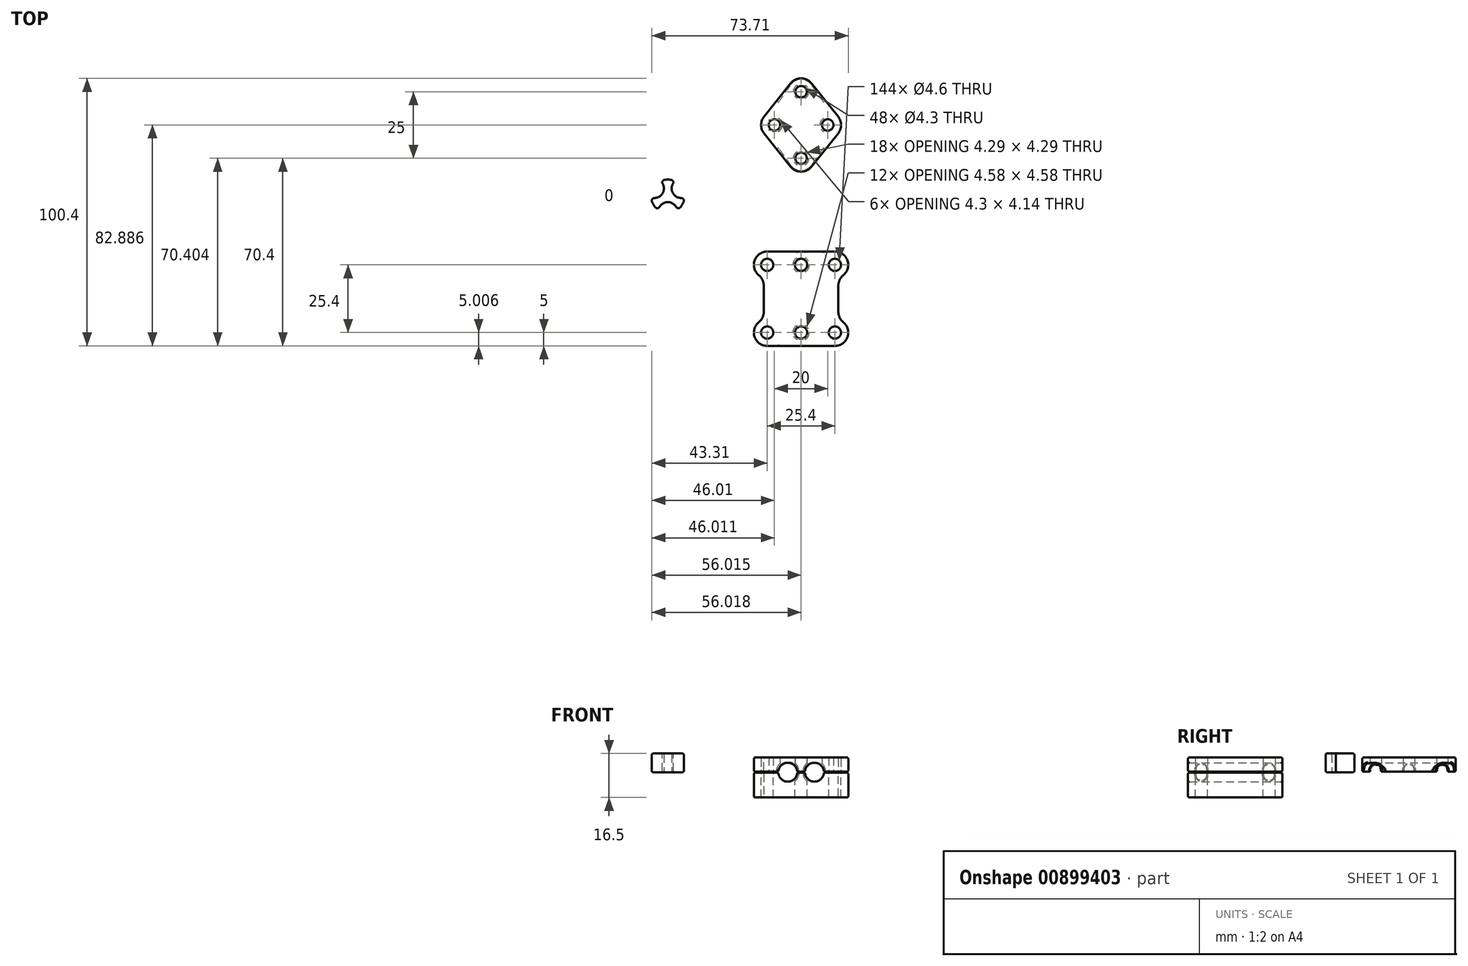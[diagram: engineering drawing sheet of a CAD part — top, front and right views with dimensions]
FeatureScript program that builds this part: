
annotation { "Feature Type Name" : "Feature", "Feature Type Description" : "" }
export const myFeature = defineFeature(function(context is Context, id is Id, definition is map)
    precondition{}
    {
        {
            var Q0;
            Q0=qCreatedBy(makeId("Top.planeOp"),FACE);
            var sketch = newSketch(context, id + "F0", { "sketchPlane" : qUnion([Q0])});
            skCircle(sketch, "E0", {"center": v(0, 45) * mm, "radius": 2.15 * mm});
            skCircle(sketch, "E1", {"center": v(-10, 32.5) * mm, "radius": 2.15 * mm});
            skCircle(sketch, "E2", {"center": v(10, 32.5) * mm, "radius": 2.15 * mm});
            skCircle(sketch, "E3", {"center": v(0, 20) * mm, "radius": 2.15 * mm});
            skArc(sketch, "E4", {"start": v(-13.9, 35.62) * mm, "mid": v(-15, 32.5) * mm, "end": v(-13.9, 29.38) * mm});
            skArc(sketch, "E5", {"start": v(-3.9, 16.88) * mm, "mid": v(0, 15) * mm, "end": v(3.9, 16.88) * mm});
            skArc(sketch, "E6", {"start": v(13.9, 29.38) * mm, "mid": v(15, 32.5) * mm, "end": v(13.9, 35.62) * mm});
            skArc(sketch, "E7", {"start": v(3.9, 48.12) * mm, "mid": v(0, 50) * mm, "end": v(-3.9, 48.12) * mm});
            skLineSegment(sketch, "E8", {"start": v(-3.9, 48.12) * mm, "end": v(-13.9, 35.62) * mm});
            skLineSegment(sketch, "E9", {"start": v(-13.9, 29.38) * mm, "end": v(-3.9, 16.88) * mm});
            skLineSegment(sketch, "E10", {"start": v(3.9, 16.88) * mm, "end": v(13.9, 29.38) * mm});
            skLineSegment(sketch, "E11", {"start": v(3.9, 48.12) * mm, "end": v(13.9, 35.62) * mm});
            skCircle(sketch, "E12", {"center": v(0, -20) * mm, "radius": 2.3 * mm});
            skCircle(sketch, "E13", {"center": v(0, -45.4) * mm, "radius": 2.3 * mm});
            skCircle(sketch, "E14", {"center": v(12.7, -20) * mm, "radius": 2.3 * mm});
            skCircle(sketch, "E15", {"center": v(12.7, -45.4) * mm, "radius": 2.3 * mm});
            skCircle(sketch, "E16", {"center": v(-12.7, -45.4) * mm, "radius": 2.3 * mm});
            skCircle(sketch, "E17", {"center": v(-12.7, -20) * mm, "radius": 2.3 * mm});
            skArc(sketch, "E18", {"start": v(-12.7, -15) * mm, "mid": v(-17.66, -19.34) * mm, "end": v(-14, -24.83) * mm});
            skArc(sketch, "E19", {"start": v(14, -24.83) * mm, "mid": v(17.66, -19.34) * mm, "end": v(12.7, -15) * mm});
            skArc(sketch, "E20", {"start": v(-14, -40.57) * mm, "mid": v(-17.66, -46.06) * mm, "end": v(-12.7, -50.4) * mm});
            skArc(sketch, "E21", {"start": v(12.7, -50.4) * mm, "mid": v(17.66, -46.06) * mm, "end": v(14, -40.57) * mm});
            skLineSegment(sketch, "E22", {"start": v(-14, -24.83) * mm, "end": v(-14, -40.57) * mm});
            skLineSegment(sketch, "E23", {"start": v(-12.7, -15) * mm, "end": v(12.7, -15) * mm});
            skLineSegment(sketch, "E24", {"start": v(14, -24.83) * mm, "end": v(14, -40.57) * mm});
            skLineSegment(sketch, "E25", {"start": v(-12.7, -50.4) * mm, "end": v(12.7, -50.4) * mm});
            skSolve(sketch);
        }
        {
            var Q0;
            Q0=makeQuery(id+"F0.imprint","IMPRINT",FACE,{"disambiguationData":[TD([[makeQuery(id+"F0.imprint","IMPRINT",EDGE,{"derivedFrom":sQuery(id+"F0.wireOp",EDGE,"E0")}),-1.0]])]});
            extrude(context, id + "F1", {"entities" : qUnion([Q0]), "depth" : 5.5 * mm, "offsetDistance" : 25 * mm, "hasSecondDirection" : true, "secondDirectionOppositeDirection" : false, "secondDirectionDepth" : 0.2 * mm});
        }
        {
            var Q0;
            Q0=makeQuery(id+"F0.imprint","IMPRINT",FACE,{"disambiguationData":[TD([[makeQuery(id+"F0.imprint","IMPRINT",EDGE,{"derivedFrom":sQuery(id+"F0.wireOp",EDGE,"E12")}),-1.0]])]});
            extrude(context, id + "F2", {"entities" : qUnion([Q0]), "depth" : 5.5 * mm, "offsetDistance" : 25 * mm, "hasSecondDirection" : true, "secondDirectionOppositeDirection" : false, "secondDirectionDepth" : 0.2 * mm});
        }
        {
            var Q0;
            Q0=makeQuery(id+"F0.imprint","IMPRINT",FACE,{"disambiguationData":[TD([[makeQuery(id+"F0.imprint","IMPRINT",EDGE,{"derivedFrom":sQuery(id+"F0.wireOp",EDGE,"E12")}),-1.0]])]});
            extrude(context, id + "F3", {"entities" : qUnion([Q0]), "oppositeDirection" : true, "depth" : 9.5 * mm, "offsetDistance" : 25 * mm, "hasSecondDirection" : true, "secondDirectionOppositeDirection" : true, "secondDirectionDepth" : 0.2 * mm});
        }
        {
            var Q0;
            Q0=qCreatedBy(makeId("Front.planeOp"),FACE);
            var sketch = newSketch(context, id + "F4", { "sketchPlane" : qUnion([Q0])});
            skCircle(sketch, "E26", {"center": v(5, 0) * mm, "radius": 3.55 * mm});
            skCircle(sketch, "E27.MirrorC", {"center": v(-5, 0) * mm, "radius": 3.55 * mm});
            skSolve(sketch);
        }
        {
            var Q0;
            Q0 = qSketchRegion(id + "F4", true);
            extrude(context, id + "F5", {"entities" : qUnion([Q0]), "operationType" : NewBodyOperationType.REMOVE, "endBound" : BoundingType.SYMMETRIC, "depth" : 200 * mm, "offsetDistance" : 25 * mm});
        }
        {
            var Q0;
            Q0=makeQuery(id+"F2.opExtrude","SWEPT_EDGE",EDGE,{"disambiguationData":[OSD([sQuery(id+"F0.wireOp",EDGE,"E18"),sQuery(id+"F0.wireOp",EDGE,"E22")])]});
            var Q1;
            Q1=makeQuery(id+"F2.opExtrude","SWEPT_EDGE",EDGE,{"disambiguationData":[OSD([sQuery(id+"F0.wireOp",EDGE,"E20"),sQuery(id+"F0.wireOp",EDGE,"E22")])]});
            var Q2;
            Q2=makeQuery(id+"F2.opExtrude","SWEPT_EDGE",EDGE,{"disambiguationData":[OSD([sQuery(id+"F0.wireOp",EDGE,"E19"),sQuery(id+"F0.wireOp",EDGE,"E24")])]});
            var Q3;
            Q3=makeQuery(id+"F2.opExtrude","SWEPT_EDGE",EDGE,{"disambiguationData":[OSD([sQuery(id+"F0.wireOp",EDGE,"E21"),sQuery(id+"F0.wireOp",EDGE,"E24")])]});
            var Q4;
            Q4=makeQuery(id+"F3.opExtrude","SWEPT_EDGE",EDGE,{"disambiguationData":[OSD([sQuery(id+"F0.wireOp",EDGE,"E18"),sQuery(id+"F0.wireOp",EDGE,"E22")])]});
            var Q5;
            Q5=makeQuery(id+"F3.opExtrude","SWEPT_EDGE",EDGE,{"disambiguationData":[OSD([sQuery(id+"F0.wireOp",EDGE,"E20"),sQuery(id+"F0.wireOp",EDGE,"E22")])]});
            var Q6;
            Q6=makeQuery(id+"F3.opExtrude","SWEPT_EDGE",EDGE,{"disambiguationData":[OSD([sQuery(id+"F0.wireOp",EDGE,"E19"),sQuery(id+"F0.wireOp",EDGE,"E24")])]});
            var Q7;
            Q7=makeQuery(id+"F3.opExtrude","SWEPT_EDGE",EDGE,{"disambiguationData":[OSD([sQuery(id+"F0.wireOp",EDGE,"E21"),sQuery(id+"F0.wireOp",EDGE,"E24")])]});
            fillet(context, id + "F6", {"entities" : qUnion([Q0, Q1, Q2, Q3, Q4, Q5, Q6, Q7]), "radius" : 5 * mm, "tangentPropagation" : true, "allowEdgeOverflow" : false});
        }
        {
            var Q0;
            Q0=makeQuery(id+"F1.opExtrude","CAP_EDGE",EDGE,{"disambiguationData":[OSD([sQuery(id+"F0.wireOp",EDGE,"E9")])],"isStart":false});
            var Q1;
            Q1=makeQuery(id+"F2.opExtrude","CAP_EDGE",EDGE,{"disambiguationData":[OSD([sQuery(id+"F0.wireOp",EDGE,"E22")])],"isStart":false});
            var Q2;
            {var subQ3=sQuery(id+"F0.wireOp",EDGE,"E12");Q2=makeQuery(id+"F5.boolean.opBoolean","COPY",FACE,{"disambiguationData":[TD([makeQuery(id+"F2.opExtrude","SWEPT_FACE",FACE,{"disambiguationData":[OSD([subQ3])]})])],"derivedFrom":makeQuery(id+"F5.opExtrude","SWEPT_FACE",FACE,{"disambiguationData":[OSD([sQuery(id+"F4.wireOp",EDGE,"E27.MirrorC")])]})});}
            var Q3;
            {var subQ3=sQuery(id+"F0.wireOp",EDGE,"E12");Q3=makeQuery(id+"F5.boolean.opBoolean","COPY",FACE,{"disambiguationData":[TD([makeQuery(id+"F2.opExtrude","SWEPT_FACE",FACE,{"disambiguationData":[OSD([subQ3])]})])],"derivedFrom":makeQuery(id+"F5.opExtrude","SWEPT_FACE",FACE,{"disambiguationData":[OSD([sQuery(id+"F4.wireOp",EDGE,"E26")])]})});}
            var Q4;
            {var subQ0=sQuery(id+"F0.wireOp",EDGE,"E12");var subQ1=sQuery(id+"F0.wireOp",EDGE,"E13");Q4=makeQuery(id+"F5.boolean.opBoolean","SPLIT",FACE,{"disambiguationData":[TD([makeQuery(id+"F2.opExtrude","SWEPT_FACE",FACE,{"disambiguationData":[OSD([subQ0])]}),makeQuery(id+"F2.opExtrude","SWEPT_FACE",FACE,{"disambiguationData":[OSD([subQ1])]}),makeQuery(id+"F5.opExtrude","SWEPT_FACE",FACE,{"disambiguationData":[OSD([sQuery(id+"F4.wireOp",EDGE,"E26")])]}),makeQuery(id+"F5.opExtrude","SWEPT_FACE",FACE,{"disambiguationData":[OSD([sQuery(id+"F4.wireOp",EDGE,"E27.MirrorC")])]})])],"derivedFrom":makeQuery(id+"F2.opExtrude","CAP_FACE",FACE,{"disambiguationData":[OSD([subQ0,subQ1,sQuery(id+"F0.wireOp",EDGE,"E14"),sQuery(id+"F0.wireOp",EDGE,"E15"),sQuery(id+"F0.wireOp",EDGE,"E16"),sQuery(id+"F0.wireOp",EDGE,"E17"),sQuery(id+"F0.wireOp",EDGE,"E18"),sQuery(id+"F0.wireOp",EDGE,"E19"),sQuery(id+"F0.wireOp",EDGE,"E20"),sQuery(id+"F0.wireOp",EDGE,"E21"),sQuery(id+"F0.wireOp",EDGE,"E22"),sQuery(id+"F0.wireOp",EDGE,"E23"),sQuery(id+"F0.wireOp",EDGE,"E24"),sQuery(id+"F0.wireOp",EDGE,"E25")])],"isStart":true})});}
            var Q5;
            {var subQ0=sQuery(id+"F0.wireOp",EDGE,"E13");var subQ1=sQuery(id+"F0.wireOp",EDGE,"E25");Q5=makeQuery(id+"F5.boolean.opBoolean","SPLIT",FACE,{"disambiguationData":[TD([makeQuery(id+"F2.opExtrude","SWEPT_FACE",FACE,{"disambiguationData":[OSD([subQ0])]}),makeQuery(id+"F2.opExtrude","SWEPT_FACE",FACE,{"disambiguationData":[OSD([subQ1])]}),makeQuery(id+"F5.opExtrude","SWEPT_FACE",FACE,{"disambiguationData":[OSD([sQuery(id+"F4.wireOp",EDGE,"E26")])]}),makeQuery(id+"F5.opExtrude","SWEPT_FACE",FACE,{"disambiguationData":[OSD([sQuery(id+"F4.wireOp",EDGE,"E27.MirrorC")])]})])],"derivedFrom":makeQuery(id+"F2.opExtrude","CAP_FACE",FACE,{"disambiguationData":[OSD([sQuery(id+"F0.wireOp",EDGE,"E12"),subQ0,sQuery(id+"F0.wireOp",EDGE,"E14"),sQuery(id+"F0.wireOp",EDGE,"E15"),sQuery(id+"F0.wireOp",EDGE,"E16"),sQuery(id+"F0.wireOp",EDGE,"E17"),sQuery(id+"F0.wireOp",EDGE,"E18"),sQuery(id+"F0.wireOp",EDGE,"E19"),sQuery(id+"F0.wireOp",EDGE,"E20"),sQuery(id+"F0.wireOp",EDGE,"E21"),sQuery(id+"F0.wireOp",EDGE,"E22"),sQuery(id+"F0.wireOp",EDGE,"E23"),sQuery(id+"F0.wireOp",EDGE,"E24"),subQ1])],"isStart":true})});}
            var Q6;
            {var subQ0=sQuery(id+"F0.wireOp",EDGE,"E12");var subQ1=sQuery(id+"F0.wireOp",EDGE,"E23");Q6=makeQuery(id+"F5.boolean.opBoolean","SPLIT",FACE,{"disambiguationData":[TD([makeQuery(id+"F2.opExtrude","SWEPT_FACE",FACE,{"disambiguationData":[OSD([subQ0])]}),makeQuery(id+"F2.opExtrude","SWEPT_FACE",FACE,{"disambiguationData":[OSD([subQ1])]}),makeQuery(id+"F5.opExtrude","SWEPT_FACE",FACE,{"disambiguationData":[OSD([sQuery(id+"F4.wireOp",EDGE,"E26")])]}),makeQuery(id+"F5.opExtrude","SWEPT_FACE",FACE,{"disambiguationData":[OSD([sQuery(id+"F4.wireOp",EDGE,"E27.MirrorC")])]})])],"derivedFrom":makeQuery(id+"F2.opExtrude","CAP_FACE",FACE,{"disambiguationData":[OSD([subQ0,sQuery(id+"F0.wireOp",EDGE,"E13"),sQuery(id+"F0.wireOp",EDGE,"E14"),sQuery(id+"F0.wireOp",EDGE,"E15"),sQuery(id+"F0.wireOp",EDGE,"E16"),sQuery(id+"F0.wireOp",EDGE,"E17"),sQuery(id+"F0.wireOp",EDGE,"E18"),sQuery(id+"F0.wireOp",EDGE,"E19"),sQuery(id+"F0.wireOp",EDGE,"E20"),sQuery(id+"F0.wireOp",EDGE,"E21"),sQuery(id+"F0.wireOp",EDGE,"E22"),subQ1,sQuery(id+"F0.wireOp",EDGE,"E24"),sQuery(id+"F0.wireOp",EDGE,"E25")])],"isStart":true})});}
            var Q7;
            {var subQ0=sQuery(id+"F0.wireOp",EDGE,"E25");var subQ1=sQuery(id+"F0.wireOp",EDGE,"E20");Q7=makeQuery(id+"F5.boolean.opBoolean","SPLIT",EDGE,{"disambiguationData":[TD([makeQuery(id+"F2.opExtrude","CAP_FACE",FACE,{"disambiguationData":[OSD([sQuery(id+"F0.wireOp",EDGE,"E12"),sQuery(id+"F0.wireOp",EDGE,"E13"),sQuery(id+"F0.wireOp",EDGE,"E14"),sQuery(id+"F0.wireOp",EDGE,"E15"),sQuery(id+"F0.wireOp",EDGE,"E16"),sQuery(id+"F0.wireOp",EDGE,"E17"),sQuery(id+"F0.wireOp",EDGE,"E18"),sQuery(id+"F0.wireOp",EDGE,"E19"),subQ1,sQuery(id+"F0.wireOp",EDGE,"E21"),sQuery(id+"F0.wireOp",EDGE,"E22"),sQuery(id+"F0.wireOp",EDGE,"E23"),sQuery(id+"F0.wireOp",EDGE,"E24"),subQ0])],"isStart":true}),makeQuery(id+"F2.opExtrude","SWEPT_FACE",FACE,{"disambiguationData":[OSD([subQ1])]}),makeQuery(id+"F2.opExtrude","SWEPT_FACE",FACE,{"disambiguationData":[OSD([subQ0])]}),makeQuery(id+"F5.opExtrude","SWEPT_FACE",FACE,{"disambiguationData":[OSD([sQuery(id+"F4.wireOp",EDGE,"E27.MirrorC")])]})])],"derivedFrom":makeQuery(id+"F2.opExtrude","CAP_EDGE",EDGE,{"disambiguationData":[OSD([subQ0])],"isStart":true})});}
            var Q8;
            Q8=makeQuery(id+"F2.opExtrude","CAP_EDGE",EDGE,{"disambiguationData":[OSD([sQuery(id+"F0.wireOp",EDGE,"E21")])],"isStart":true});
            var Q9;
            {var subQ6=sQuery(id+"F0.wireOp",EDGE,"E0");Q9=makeQuery(id+"F5.boolean.opBoolean","COPY",FACE,{"disambiguationData":[TD([makeQuery(id+"F1.opExtrude","SWEPT_FACE",FACE,{"disambiguationData":[OSD([subQ6])]})])],"derivedFrom":makeQuery(id+"F5.opExtrude","SWEPT_FACE",FACE,{"disambiguationData":[OSD([sQuery(id+"F4.wireOp",EDGE,"E26")])]})});}
            var Q10;
            {var subQ6=sQuery(id+"F0.wireOp",EDGE,"E0");Q10=makeQuery(id+"F5.boolean.opBoolean","COPY",FACE,{"disambiguationData":[TD([makeQuery(id+"F1.opExtrude","SWEPT_FACE",FACE,{"disambiguationData":[OSD([subQ6])]})])],"derivedFrom":makeQuery(id+"F5.opExtrude","SWEPT_FACE",FACE,{"disambiguationData":[OSD([sQuery(id+"F4.wireOp",EDGE,"E27.MirrorC")])]})});}
            var Q11;
            {var subQ0=sQuery(id+"F0.wireOp",EDGE,"E3");var subQ1=sQuery(id+"F0.wireOp",EDGE,"E5");Q11=makeQuery(id+"F5.boolean.opBoolean","SPLIT",FACE,{"disambiguationData":[TD([makeQuery(id+"F1.opExtrude","SWEPT_FACE",FACE,{"disambiguationData":[OSD([subQ0])]}),makeQuery(id+"F1.opExtrude","SWEPT_FACE",FACE,{"disambiguationData":[OSD([subQ1])]}),makeQuery(id+"F5.opExtrude","SWEPT_FACE",FACE,{"disambiguationData":[OSD([sQuery(id+"F4.wireOp",EDGE,"E26")])]}),makeQuery(id+"F5.opExtrude","SWEPT_FACE",FACE,{"disambiguationData":[OSD([sQuery(id+"F4.wireOp",EDGE,"E27.MirrorC")])]})])],"derivedFrom":makeQuery(id+"F1.opExtrude","CAP_FACE",FACE,{"disambiguationData":[OSD([sQuery(id+"F0.wireOp",EDGE,"E0"),sQuery(id+"F0.wireOp",EDGE,"E1"),sQuery(id+"F0.wireOp",EDGE,"E2"),subQ0,sQuery(id+"F0.wireOp",EDGE,"E4"),subQ1,sQuery(id+"F0.wireOp",EDGE,"E6"),sQuery(id+"F0.wireOp",EDGE,"E7"),sQuery(id+"F0.wireOp",EDGE,"E8"),sQuery(id+"F0.wireOp",EDGE,"E9"),sQuery(id+"F0.wireOp",EDGE,"E10"),sQuery(id+"F0.wireOp",EDGE,"E11")])],"isStart":true})});}
            var Q12;
            {var subQ0=sQuery(id+"F0.wireOp",EDGE,"E0");var subQ1=sQuery(id+"F0.wireOp",EDGE,"E3");Q12=makeQuery(id+"F5.boolean.opBoolean","SPLIT",FACE,{"disambiguationData":[TD([makeQuery(id+"F1.opExtrude","SWEPT_FACE",FACE,{"disambiguationData":[OSD([subQ0])]}),makeQuery(id+"F1.opExtrude","SWEPT_FACE",FACE,{"disambiguationData":[OSD([subQ1])]}),makeQuery(id+"F5.opExtrude","SWEPT_FACE",FACE,{"disambiguationData":[OSD([sQuery(id+"F4.wireOp",EDGE,"E26")])]}),makeQuery(id+"F5.opExtrude","SWEPT_FACE",FACE,{"disambiguationData":[OSD([sQuery(id+"F4.wireOp",EDGE,"E27.MirrorC")])]})])],"derivedFrom":makeQuery(id+"F1.opExtrude","CAP_FACE",FACE,{"disambiguationData":[OSD([subQ0,sQuery(id+"F0.wireOp",EDGE,"E1"),sQuery(id+"F0.wireOp",EDGE,"E2"),subQ1,sQuery(id+"F0.wireOp",EDGE,"E4"),sQuery(id+"F0.wireOp",EDGE,"E5"),sQuery(id+"F0.wireOp",EDGE,"E6"),sQuery(id+"F0.wireOp",EDGE,"E7"),sQuery(id+"F0.wireOp",EDGE,"E8"),sQuery(id+"F0.wireOp",EDGE,"E9"),sQuery(id+"F0.wireOp",EDGE,"E10"),sQuery(id+"F0.wireOp",EDGE,"E11")])],"isStart":true})});}
            var Q13;
            {var subQ0=sQuery(id+"F0.wireOp",EDGE,"E0");var subQ1=sQuery(id+"F0.wireOp",EDGE,"E7");Q13=makeQuery(id+"F5.boolean.opBoolean","SPLIT",FACE,{"disambiguationData":[TD([makeQuery(id+"F1.opExtrude","SWEPT_FACE",FACE,{"disambiguationData":[OSD([subQ0])]}),makeQuery(id+"F1.opExtrude","SWEPT_FACE",FACE,{"disambiguationData":[OSD([subQ1])]}),makeQuery(id+"F5.opExtrude","SWEPT_FACE",FACE,{"disambiguationData":[OSD([sQuery(id+"F4.wireOp",EDGE,"E26")])]}),makeQuery(id+"F5.opExtrude","SWEPT_FACE",FACE,{"disambiguationData":[OSD([sQuery(id+"F4.wireOp",EDGE,"E27.MirrorC")])]})])],"derivedFrom":makeQuery(id+"F1.opExtrude","CAP_FACE",FACE,{"disambiguationData":[OSD([subQ0,sQuery(id+"F0.wireOp",EDGE,"E1"),sQuery(id+"F0.wireOp",EDGE,"E2"),sQuery(id+"F0.wireOp",EDGE,"E3"),sQuery(id+"F0.wireOp",EDGE,"E4"),sQuery(id+"F0.wireOp",EDGE,"E5"),sQuery(id+"F0.wireOp",EDGE,"E6"),subQ1,sQuery(id+"F0.wireOp",EDGE,"E8"),sQuery(id+"F0.wireOp",EDGE,"E9"),sQuery(id+"F0.wireOp",EDGE,"E10"),sQuery(id+"F0.wireOp",EDGE,"E11")])],"isStart":true})});}
            var Q14;
            Q14=makeQuery(id+"F1.opExtrude","CAP_EDGE",EDGE,{"disambiguationData":[OSD([sQuery(id+"F0.wireOp",EDGE,"E10")])],"isStart":true});
            var Q15;
            Q15=makeQuery(id+"F1.opExtrude","CAP_EDGE",EDGE,{"disambiguationData":[OSD([sQuery(id+"F0.wireOp",EDGE,"E9")])],"isStart":true});
            var Q16;
            Q16=makeQuery(id+"F1.opExtrude","CAP_EDGE",EDGE,{"disambiguationData":[OSD([sQuery(id+"F0.wireOp",EDGE,"E2")])],"isStart":true});
            var Q17;
            Q17=makeQuery(id+"F1.opExtrude","CAP_EDGE",EDGE,{"disambiguationData":[OSD([sQuery(id+"F0.wireOp",EDGE,"E1")])],"isStart":true});
            var Q18;
            Q18=makeQuery(id+"F2.opExtrude","CAP_EDGE",EDGE,{"disambiguationData":[OSD([sQuery(id+"F0.wireOp",EDGE,"E14")])],"isStart":true});
            var Q19;
            Q19=makeQuery(id+"F2.opExtrude","CAP_EDGE",EDGE,{"disambiguationData":[OSD([sQuery(id+"F0.wireOp",EDGE,"E15")])],"isStart":true});
            var Q20;
            Q20=makeQuery(id+"F2.opExtrude","CAP_EDGE",EDGE,{"disambiguationData":[OSD([sQuery(id+"F0.wireOp",EDGE,"E17")])],"isStart":true});
            var Q21;
            Q21=makeQuery(id+"F2.opExtrude","CAP_EDGE",EDGE,{"disambiguationData":[OSD([sQuery(id+"F0.wireOp",EDGE,"E16")])],"isStart":true});
            var Q22;
            Q22=makeQuery(id+"F3.opExtrude","CAP_EDGE",EDGE,{"disambiguationData":[OSD([sQuery(id+"F0.wireOp",EDGE,"E19")])],"isStart":false});
            var Q23;
            Q23=makeQuery(id+"F3.opExtrude","CAP_EDGE",EDGE,{"disambiguationData":[OSD([sQuery(id+"F0.wireOp",EDGE,"E19")])],"isStart":true});
            var Q24;
            Q24=makeQuery(id+"F3.opExtrude","CAP_EDGE",EDGE,{"disambiguationData":[OSD([sQuery(id+"F0.wireOp",EDGE,"E18")])],"isStart":true});
            var Q25;
            {var subQ3=sQuery(id+"F0.wireOp",EDGE,"E12");Q25=makeQuery(id+"F5.boolean.opBoolean","COPY",FACE,{"disambiguationData":[TD([makeQuery(id+"F3.opExtrude","SWEPT_FACE",FACE,{"disambiguationData":[OSD([subQ3])]})])],"derivedFrom":makeQuery(id+"F5.opExtrude","SWEPT_FACE",FACE,{"disambiguationData":[OSD([sQuery(id+"F4.wireOp",EDGE,"E27.MirrorC")])]})});}
            var Q26;
            {var subQ3=sQuery(id+"F0.wireOp",EDGE,"E12");Q26=makeQuery(id+"F5.boolean.opBoolean","COPY",FACE,{"disambiguationData":[TD([makeQuery(id+"F3.opExtrude","SWEPT_FACE",FACE,{"disambiguationData":[OSD([subQ3])]})])],"derivedFrom":makeQuery(id+"F5.opExtrude","SWEPT_FACE",FACE,{"disambiguationData":[OSD([sQuery(id+"F4.wireOp",EDGE,"E26")])]})});}
            var Q27;
            {var subQ0=sQuery(id+"F0.wireOp",EDGE,"E13");var subQ1=sQuery(id+"F0.wireOp",EDGE,"E25");Q27=makeQuery(id+"F5.boolean.opBoolean","SPLIT",FACE,{"disambiguationData":[TD([makeQuery(id+"F3.opExtrude","SWEPT_FACE",FACE,{"disambiguationData":[OSD([subQ0])]}),makeQuery(id+"F3.opExtrude","SWEPT_FACE",FACE,{"disambiguationData":[OSD([subQ1])]}),makeQuery(id+"F5.opExtrude","SWEPT_FACE",FACE,{"disambiguationData":[OSD([sQuery(id+"F4.wireOp",EDGE,"E26")])]}),makeQuery(id+"F5.opExtrude","SWEPT_FACE",FACE,{"disambiguationData":[OSD([sQuery(id+"F4.wireOp",EDGE,"E27.MirrorC")])]})])],"derivedFrom":makeQuery(id+"F3.opExtrude","CAP_FACE",FACE,{"disambiguationData":[OSD([sQuery(id+"F0.wireOp",EDGE,"E12"),subQ0,sQuery(id+"F0.wireOp",EDGE,"E14"),sQuery(id+"F0.wireOp",EDGE,"E15"),sQuery(id+"F0.wireOp",EDGE,"E16"),sQuery(id+"F0.wireOp",EDGE,"E17"),sQuery(id+"F0.wireOp",EDGE,"E18"),sQuery(id+"F0.wireOp",EDGE,"E19"),sQuery(id+"F0.wireOp",EDGE,"E20"),sQuery(id+"F0.wireOp",EDGE,"E21"),sQuery(id+"F0.wireOp",EDGE,"E22"),sQuery(id+"F0.wireOp",EDGE,"E23"),sQuery(id+"F0.wireOp",EDGE,"E24"),subQ1])],"isStart":true})});}
            var Q28;
            {var subQ0=sQuery(id+"F0.wireOp",EDGE,"E12");var subQ1=sQuery(id+"F0.wireOp",EDGE,"E13");Q28=makeQuery(id+"F5.boolean.opBoolean","SPLIT",FACE,{"disambiguationData":[TD([makeQuery(id+"F3.opExtrude","SWEPT_FACE",FACE,{"disambiguationData":[OSD([subQ0])]}),makeQuery(id+"F3.opExtrude","SWEPT_FACE",FACE,{"disambiguationData":[OSD([subQ1])]}),makeQuery(id+"F5.opExtrude","SWEPT_FACE",FACE,{"disambiguationData":[OSD([sQuery(id+"F4.wireOp",EDGE,"E26")])]}),makeQuery(id+"F5.opExtrude","SWEPT_FACE",FACE,{"disambiguationData":[OSD([sQuery(id+"F4.wireOp",EDGE,"E27.MirrorC")])]})])],"derivedFrom":makeQuery(id+"F3.opExtrude","CAP_FACE",FACE,{"disambiguationData":[OSD([subQ0,subQ1,sQuery(id+"F0.wireOp",EDGE,"E14"),sQuery(id+"F0.wireOp",EDGE,"E15"),sQuery(id+"F0.wireOp",EDGE,"E16"),sQuery(id+"F0.wireOp",EDGE,"E17"),sQuery(id+"F0.wireOp",EDGE,"E18"),sQuery(id+"F0.wireOp",EDGE,"E19"),sQuery(id+"F0.wireOp",EDGE,"E20"),sQuery(id+"F0.wireOp",EDGE,"E21"),sQuery(id+"F0.wireOp",EDGE,"E22"),sQuery(id+"F0.wireOp",EDGE,"E23"),sQuery(id+"F0.wireOp",EDGE,"E24"),sQuery(id+"F0.wireOp",EDGE,"E25")])],"isStart":true})});}
            var Q29;
            {var subQ0=sQuery(id+"F0.wireOp",EDGE,"E12");var subQ1=sQuery(id+"F0.wireOp",EDGE,"E23");Q29=makeQuery(id+"F5.boolean.opBoolean","SPLIT",FACE,{"disambiguationData":[TD([makeQuery(id+"F3.opExtrude","SWEPT_FACE",FACE,{"disambiguationData":[OSD([subQ0])]}),makeQuery(id+"F3.opExtrude","SWEPT_FACE",FACE,{"disambiguationData":[OSD([subQ1])]}),makeQuery(id+"F5.opExtrude","SWEPT_FACE",FACE,{"disambiguationData":[OSD([sQuery(id+"F4.wireOp",EDGE,"E26")])]}),makeQuery(id+"F5.opExtrude","SWEPT_FACE",FACE,{"disambiguationData":[OSD([sQuery(id+"F4.wireOp",EDGE,"E27.MirrorC")])]})])],"derivedFrom":makeQuery(id+"F3.opExtrude","CAP_FACE",FACE,{"disambiguationData":[OSD([subQ0,sQuery(id+"F0.wireOp",EDGE,"E13"),sQuery(id+"F0.wireOp",EDGE,"E14"),sQuery(id+"F0.wireOp",EDGE,"E15"),sQuery(id+"F0.wireOp",EDGE,"E16"),sQuery(id+"F0.wireOp",EDGE,"E17"),sQuery(id+"F0.wireOp",EDGE,"E18"),sQuery(id+"F0.wireOp",EDGE,"E19"),sQuery(id+"F0.wireOp",EDGE,"E20"),sQuery(id+"F0.wireOp",EDGE,"E21"),sQuery(id+"F0.wireOp",EDGE,"E22"),subQ1,sQuery(id+"F0.wireOp",EDGE,"E24"),sQuery(id+"F0.wireOp",EDGE,"E25")])],"isStart":true})});}
            var Q30;
            Q30=makeQuery(id+"F3.opExtrude","CAP_EDGE",EDGE,{"disambiguationData":[OSD([sQuery(id+"F0.wireOp",EDGE,"E17")])],"isStart":true});
            var Q31;
            Q31=makeQuery(id+"F3.opExtrude","CAP_EDGE",EDGE,{"disambiguationData":[OSD([sQuery(id+"F0.wireOp",EDGE,"E16")])],"isStart":true});
            var Q32;
            Q32=makeQuery(id+"F3.opExtrude","CAP_EDGE",EDGE,{"disambiguationData":[OSD([sQuery(id+"F0.wireOp",EDGE,"E15")])],"isStart":true});
            var Q33;
            Q33=makeQuery(id+"F3.opExtrude","CAP_EDGE",EDGE,{"disambiguationData":[OSD([sQuery(id+"F0.wireOp",EDGE,"E14")])],"isStart":true});
            fillet(context, id + "F7", {"entities" : qUnion([Q0, Q1, Q2, Q3, Q4, Q5, Q6, Q7, Q8, Q9, Q10, Q11, Q12, Q13, Q14, Q15, Q16, Q17, Q18, Q19, Q20, Q21, Q22, Q23, Q24, Q25, Q26, Q27, Q28, Q29, Q30, Q31, Q32, Q33]), "radius" : 0.5 * mm, "tangentPropagation" : true, "allowEdgeOverflow" : false});
        }
        {
            var Q0;
            Q0=qCreatedBy(makeId("Top.planeOp"),FACE);
            var sketch = newSketch(context, id + "F8", { "sketchPlane" : qUnion([Q0])});
            skArc(sketch, "E28", {"start": v(-56.57, 5.48) * mm, "mid": v(-51.93, 6.89) * mm, "end": v(-53.03, 11.61) * mm});
            skArc(sketch, "E29", {"start": v(-46.97, 11.61) * mm, "mid": v(-48.07, 6.89) * mm, "end": v(-43.43, 5.48) * mm});
            skArc(sketch, "E30", {"start": v(-46.46, 0.23) * mm, "mid": v(-50, 3.55) * mm, "end": v(-53.54, 0.23) * mm});
            skArc(sketch, "E31", {"start": v(-46.97, 11.61) * mm, "mid": v(-50, 12) * mm, "end": v(-53.03, 11.61) * mm});
            skArc(sketch, "E32", {"start": v(-46.46, 0.23) * mm, "mid": v(-44.6, 2.66) * mm, "end": v(-43.43, 5.48) * mm});
            skArc(sketch, "E33", {"start": v(-56.57, 5.48) * mm, "mid": v(-55.4, 2.66) * mm, "end": v(-53.54, 0.23) * mm});
            skSolve(sketch);
        }
        {
            var Q0;
            Q0 = qSketchRegion(id + "F8", true);
            extrude(context, id + "F9", {"entities" : qUnion([Q0]), "depth" : 7 * mm, "offsetDistance" : 25 * mm});
        }
        {
            var Q0;
            Q0=makeQuery(id+"F9.opExtrude","SWEPT_EDGE",EDGE,{"disambiguationData":[OSD([sQuery(id+"F8.wireOp",EDGE,"E28"),sQuery(id+"F8.wireOp",EDGE,"E33")])]});
            var Q1;
            Q1=makeQuery(id+"F9.opExtrude","SWEPT_EDGE",EDGE,{"disambiguationData":[OSD([sQuery(id+"F8.wireOp",EDGE,"E30"),sQuery(id+"F8.wireOp",EDGE,"E33")])]});
            var Q2;
            Q2=makeQuery(id+"F9.opExtrude","SWEPT_EDGE",EDGE,{"disambiguationData":[OSD([sQuery(id+"F8.wireOp",EDGE,"E30"),sQuery(id+"F8.wireOp",EDGE,"E32")])]});
            var Q3;
            Q3=makeQuery(id+"F9.opExtrude","SWEPT_EDGE",EDGE,{"disambiguationData":[OSD([sQuery(id+"F8.wireOp",EDGE,"E29"),sQuery(id+"F8.wireOp",EDGE,"E32")])]});
            var Q4;
            Q4=makeQuery(id+"F9.opExtrude","SWEPT_EDGE",EDGE,{"disambiguationData":[OSD([sQuery(id+"F8.wireOp",EDGE,"E29"),sQuery(id+"F8.wireOp",EDGE,"E31")])]});
            var Q5;
            Q5=makeQuery(id+"F9.opExtrude","SWEPT_EDGE",EDGE,{"disambiguationData":[OSD([sQuery(id+"F8.wireOp",EDGE,"E28"),sQuery(id+"F8.wireOp",EDGE,"E31")])]});
            fillet(context, id + "F10", {"entities" : qUnion([Q0, Q1, Q2, Q3, Q4, Q5]), "radius" : 1 * mm, "tangentPropagation" : true, "allowEdgeOverflow" : false});
        }
        {
            var Q0;
            Q0=makeQuery(id+"F9.opExtrude","CAP_EDGE",EDGE,{"disambiguationData":[OSD([sQuery(id+"F8.wireOp",EDGE,"E30")])],"isStart":false});
            var Q1;
            Q1=makeQuery(id+"F9.opExtrude","CAP_EDGE",EDGE,{"disambiguationData":[OSD([sQuery(id+"F8.wireOp",EDGE,"E30")])],"isStart":true});
            fillet(context, id + "F11", {"entities" : qUnion([Q0, Q1]), "radius" : 0.5 * mm, "tangentPropagation" : true, "allowEdgeOverflow" : false});
        }
    });
